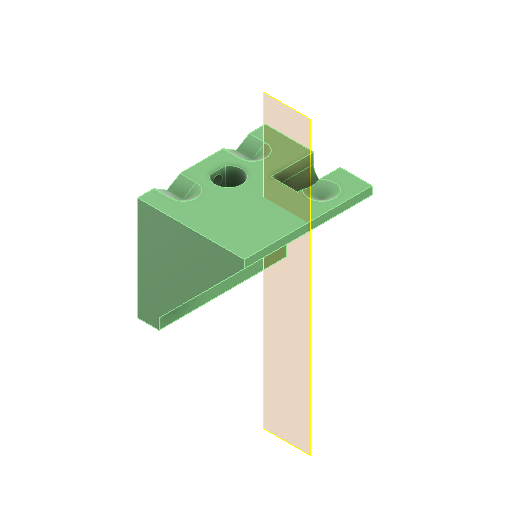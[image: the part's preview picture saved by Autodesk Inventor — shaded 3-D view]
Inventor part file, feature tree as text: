
AUTODESK INVENTOR PART (.ipt)
format: ipt  version: 2022 (Build 260153000, 153)  size: 248,320 bytes
history: native  units: mm
features: sketch x9, extrude x8, reference x5, other x3, plane x1, hole x1, projected_geometry x1
ambient origin geometry x8: Origin, YZ Plane, XZ Plane, XY Plane, X Axis, Y Axis, Z Axis, Center Point
bodies: Volumenkörper1 (feature_tree)
feature tree (28):
  plane  "Arbeitsebene1"
  extrude  "Extrusion1"  TaperAngle=45.0deg  [1 undecoded]
  extrude  "Extrusion2"  Depth=0.5mm
  extrude  "Extrusion3"  Depth=24.0mm TaperAngle=0.0deg
  hole  "Bohrung2"  [1 undecoded]
  extrude  "Extrusion7"  Depth=24.0mm TaperAngle=0.0deg
  extrude  "Extrusion8"  Depth=19.0mm
  extrude  "Extrusion9"  Depth=1.0mm
  extrude  "Extrusion10"  Depth=2.0mm
  extrude  "Extrusion11"  Depth=1.9mm
  sketch  "Skizze1"  dims[d0=22.0mm d1=45.0deg]
  reference  "Referenz1"
  sketch  "Skizze3"  dims[d2=3.35mm d3=0.5mm]
  reference  "Referenz3"
  sketch  "Skizze4"  dims[d4=2.0mm d5=24.0mm d6=0.0mm]
  sketch  "Skizze8"  dims[d7=2.0mm d8=1.0mm]
  reference  "Referenz4"
  sketch  "Skizze9"  dims[d16=12.0mm d17=24.0mm d18=0.0mm]
  reference  "Referenz5"
  sketch  "Skizze10"  dims[d19=19.0mm d20=19.0mm]
  sketch  "Skizze11"  dims[d21=0.5mm d22=0.0mm d29=1.0mm]
  reference  "Referenz6"
  sketch  "Skizze12"  dims[d32=5.0mm d33=6.0mm d34=4.0mm d35=2.0mm d36=90.0deg d37=0.01mm d38=20.594885mm d39=2.0mm]
  sketch  "Skizze13"  dims[d40=8.0mm d41=0.0mm d42=1.9mm d43=8.0mm d44=0.0mm d45=5.0mm d46=8.0mm d47=0.0mm d48=1.9mm d49=8.0mm d50=0.0mm d51=3.0mm d52=0.0mm d30=0.5mm d31=0.872665mm]
  projected_geometry  "Projizierte Kontur3"
  other  "Assembly_Autofocus_ke400_adjustable.iam"
  other  "20_Cube_Insert_Autofocus_KES400a_mirrorinsert:1"
  other  "Baugruppe1"
note: 2 required parameter values undecoded (feature->parameter linkage not recoverable at this tier; creation-order binding heuristic only, values carry confidence <= 0.55)
